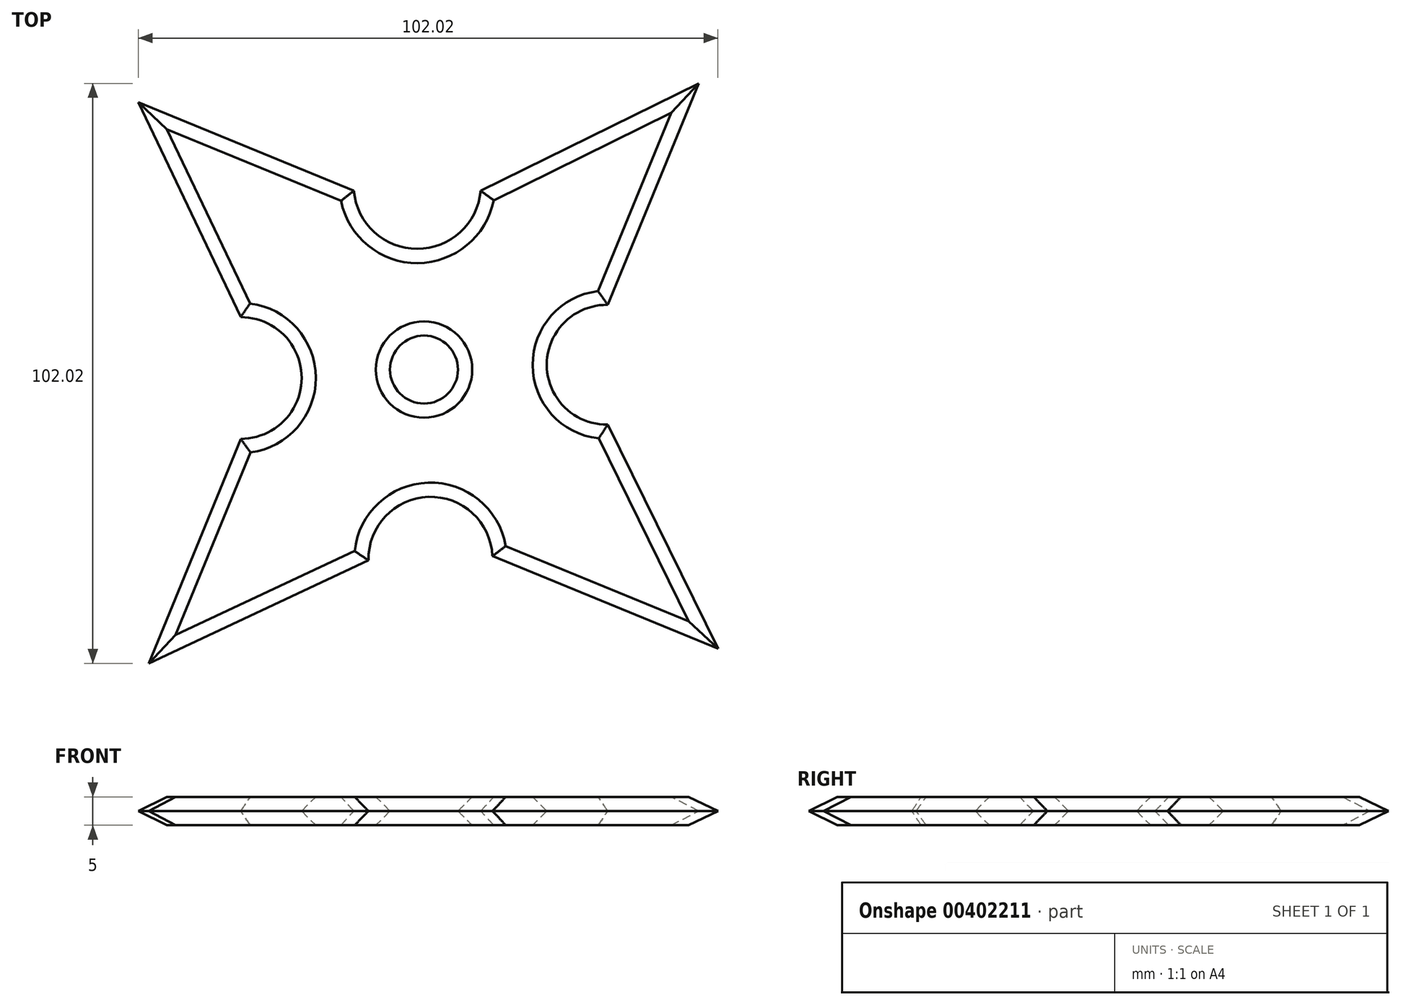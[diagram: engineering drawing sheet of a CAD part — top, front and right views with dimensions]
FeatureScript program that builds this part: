
annotation { "Feature Type Name" : "Feature", "Feature Type Description" : "" }
export const myFeature = defineFeature(function(context is Context, id is Id, definition is map)
    precondition{}
    {
        {
            var Q0;
            Q0=qCreatedBy(makeId("Top.planeOp"),FACE);
            var sketch = newSketch(context, id + "F0", { "sketchPlane" : qUnion([Q0])});
            skLineSegment(sketch, "E0", {"start": v(60, 120) * mm, "end": v(60, 0) * mm, "construction": true});
            skLineSegment(sketch, "E1", {"start": v(11.55, 9.53) * mm, "end": v(50.24, 27.66) * mm});
            skLineSegment(sketch, "E2", {"start": v(50.24, 27.66) * mm, "end": v(11.55, 9.53) * mm});
            skLineSegment(sketch, "E3", {"start": v(11.55, 9.53) * mm, "end": v(27.76, 49.03) * mm});
            skLineSegment(sketch, "E4", {"start": v(27.76, 70.43) * mm, "end": v(9.72, 108.23) * mm});
            skLineSegment(sketch, "E5", {"start": v(9.72, 108.23) * mm, "end": v(47.66, 92.66) * mm});
            skLineSegment(sketch, "E6", {"start": v(69.97, 92.66) * mm, "end": v(108.31, 111.55) * mm});
            skLineSegment(sketch, "E7", {"start": v(108.31, 111.55) * mm, "end": v(92.32, 72.6) * mm});
            skLineSegment(sketch, "E8", {"start": v(92.32, 51.52) * mm, "end": v(111.74, 12.12) * mm});
            skLineSegment(sketch, "E9", {"start": v(111.74, 12.12) * mm, "end": v(72.05, 28.41) * mm});
            skArc(sketch, "E10", {"start": v(27.76, 49.03) * mm, "mid": v(38.47, 59.73) * mm, "end": v(27.76, 70.43) * mm});
            skArc(sketch, "E11", {"start": v(47.66, 92.66) * mm, "mid": v(58.82, 82.44) * mm, "end": v(69.97, 92.66) * mm});
            skArc(sketch, "E12", {"start": v(92.32, 72.6) * mm, "mid": v(81.62, 62.06) * mm, "end": v(92.32, 51.52) * mm});
            skArc(sketch, "E13", {"start": v(72.05, 28.41) * mm, "mid": v(60.77, 38.81) * mm, "end": v(50.24, 27.66) * mm});
            skCircle(sketch, "E14", {"center": v(60, 61.21) * mm, "radius": 5.98 * mm});
            skPoint(sketch, "E14.first.point", {"position": v(60, 67.2) * mm});
            skPoint(sketch, "E14.second.point", {"position": v(60, 55.23) * mm});
            skPoint(sketch, "E14.third.point", {"position": v(65.98, 61.08) * mm});
            skSolve(sketch);
        }
        {
            var Q0;
            Q0 = qSketchRegion(id + "F0", true);
            extrude(context, id + "F1", {"entities" : qUnion([Q0]), "depth" : 5 * mm});
        }
        {
            var Q0;
            Q0=makeQuery(id+"F1.opExtrude","CAP_FACE",FACE,{"disambiguationData":[OSD([sQuery(id+"F0.wireOp",EDGE,"E2"),sQuery(id+"F0.wireOp",EDGE,"E3"),sQuery(id+"F0.wireOp",EDGE,"E4"),sQuery(id+"F0.wireOp",EDGE,"E5"),sQuery(id+"F0.wireOp",EDGE,"E6"),sQuery(id+"F0.wireOp",EDGE,"E7"),sQuery(id+"F0.wireOp",EDGE,"E8"),sQuery(id+"F0.wireOp",EDGE,"E9"),sQuery(id+"F0.wireOp",EDGE,"E10"),sQuery(id+"F0.wireOp",EDGE,"E11"),sQuery(id+"F0.wireOp",EDGE,"E12"),sQuery(id+"F0.wireOp",EDGE,"E13"),sQuery(id+"F0.wireOp",EDGE,"E14")])],"isStart":false});
            var Q1;
            Q1=makeQuery(id+"F1.opExtrude","CAP_FACE",FACE,{"disambiguationData":[OSD([sQuery(id+"F0.wireOp",EDGE,"E2"),sQuery(id+"F0.wireOp",EDGE,"E3"),sQuery(id+"F0.wireOp",EDGE,"E4"),sQuery(id+"F0.wireOp",EDGE,"E5"),sQuery(id+"F0.wireOp",EDGE,"E6"),sQuery(id+"F0.wireOp",EDGE,"E7"),sQuery(id+"F0.wireOp",EDGE,"E8"),sQuery(id+"F0.wireOp",EDGE,"E9"),sQuery(id+"F0.wireOp",EDGE,"E10"),sQuery(id+"F0.wireOp",EDGE,"E11"),sQuery(id+"F0.wireOp",EDGE,"E12"),sQuery(id+"F0.wireOp",EDGE,"E13"),sQuery(id+"F0.wireOp",EDGE,"E14")])],"isStart":true});
            chamfer(context, id + "F2", {"entities" : qUnion([Q0, Q1]), "width" : 2.5 * mm, "tangentPropagation" : true});
        }
    });
